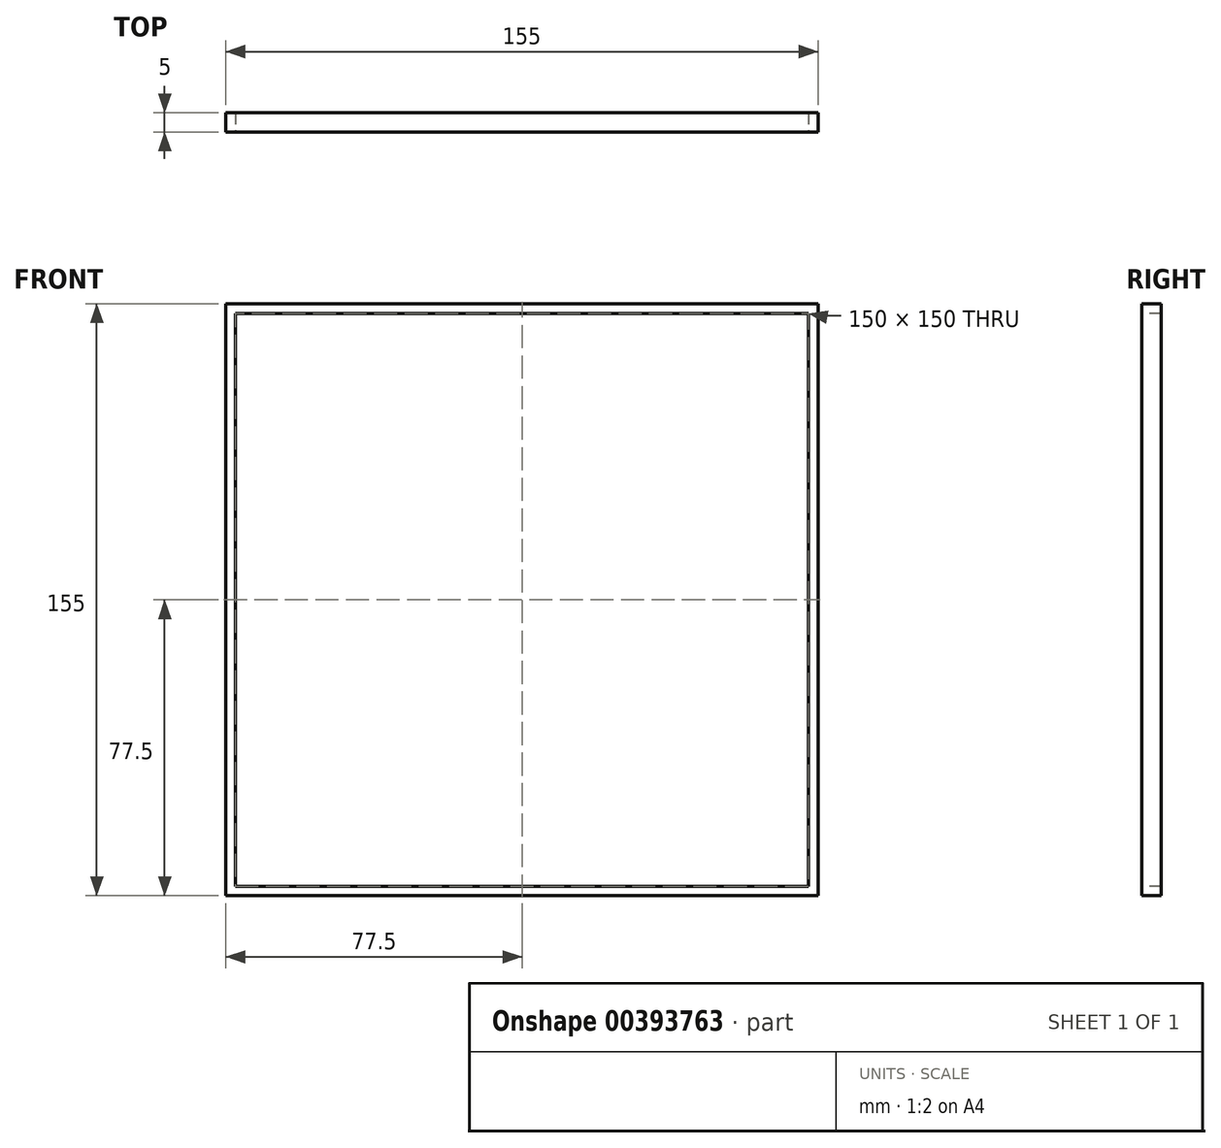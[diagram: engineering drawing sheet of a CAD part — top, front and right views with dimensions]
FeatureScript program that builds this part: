
annotation { "Feature Type Name" : "Feature", "Feature Type Description" : "" }
export const myFeature = defineFeature(function(context is Context, id is Id, definition is map)
    precondition{}
    {
        {
            var Q0;
            Q0=qCreatedBy(makeId("Front.planeOp"),FACE);
            var sketch = newSketch(context, id + "F0", { "sketchPlane" : qUnion([Q0])});
            skLineSegment(sketch, "E0.bottom", {"start": v(77.5, 77.5) * mm, "end": v(-77.5, 77.5) * mm});
            skLineSegment(sketch, "E0.top", {"start": v(77.5, -77.5) * mm, "end": v(-77.5, -77.5) * mm});
            skLineSegment(sketch, "E0.left", {"start": v(77.5, 77.5) * mm, "end": v(77.5, -77.5) * mm});
            skLineSegment(sketch, "E0.right", {"start": v(-77.5, 77.5) * mm, "end": v(-77.5, -77.5) * mm});
            skPoint(sketch, "E0.middle", {"position": v(0, 0) * mm});
            skSolve(sketch);
        }
        {
            var Q0;
            Q0 = qSketchRegion(id + "F0", true);
            extrude(context, id + "F1", {"entities" : qUnion([Q0]), "depth" : 5 * mm});
        }
        {
            var Q0;
            Q0=makeQuery(id+"F1.opExtrude","CAP_FACE",FACE,{"disambiguationData":[OSD([sQuery(id+"F0.wireOp",EDGE,"E0.bottom"),sQuery(id+"F0.wireOp",EDGE,"E0.top"),sQuery(id+"F0.wireOp",EDGE,"E0.left"),sQuery(id+"F0.wireOp",EDGE,"E0.right")])],"isStart":false});
            var sketch = newSketch(context, id + "F2", { "sketchPlane" : qUnion([Q0])});
            skPoint(sketch, "E1.middle", {"position": v(11.2, 0) * mm});
            skLineSegment(sketch, "E2.bottom", {"start": v(75, 75) * mm, "end": v(-75, 75) * mm});
            skLineSegment(sketch, "E2.top", {"start": v(75, -75) * mm, "end": v(-75, -75) * mm});
            skLineSegment(sketch, "E2.left", {"start": v(75, 75) * mm, "end": v(75, -75) * mm});
            skLineSegment(sketch, "E2.right", {"start": v(-75, 75) * mm, "end": v(-75, -75) * mm});
            skPoint(sketch, "E2.middle", {"position": v(0, 0) * mm});
            skSolve(sketch);
        }
        {
            var Q0;
            Q0 = qSketchRegion(id + "F2", true);
            extrude(context, id + "F3", {"entities" : qUnion([Q0]), "operationType" : NewBodyOperationType.REMOVE, "oppositeDirection" : true, "depth" : 5 * mm});
        }
    });
